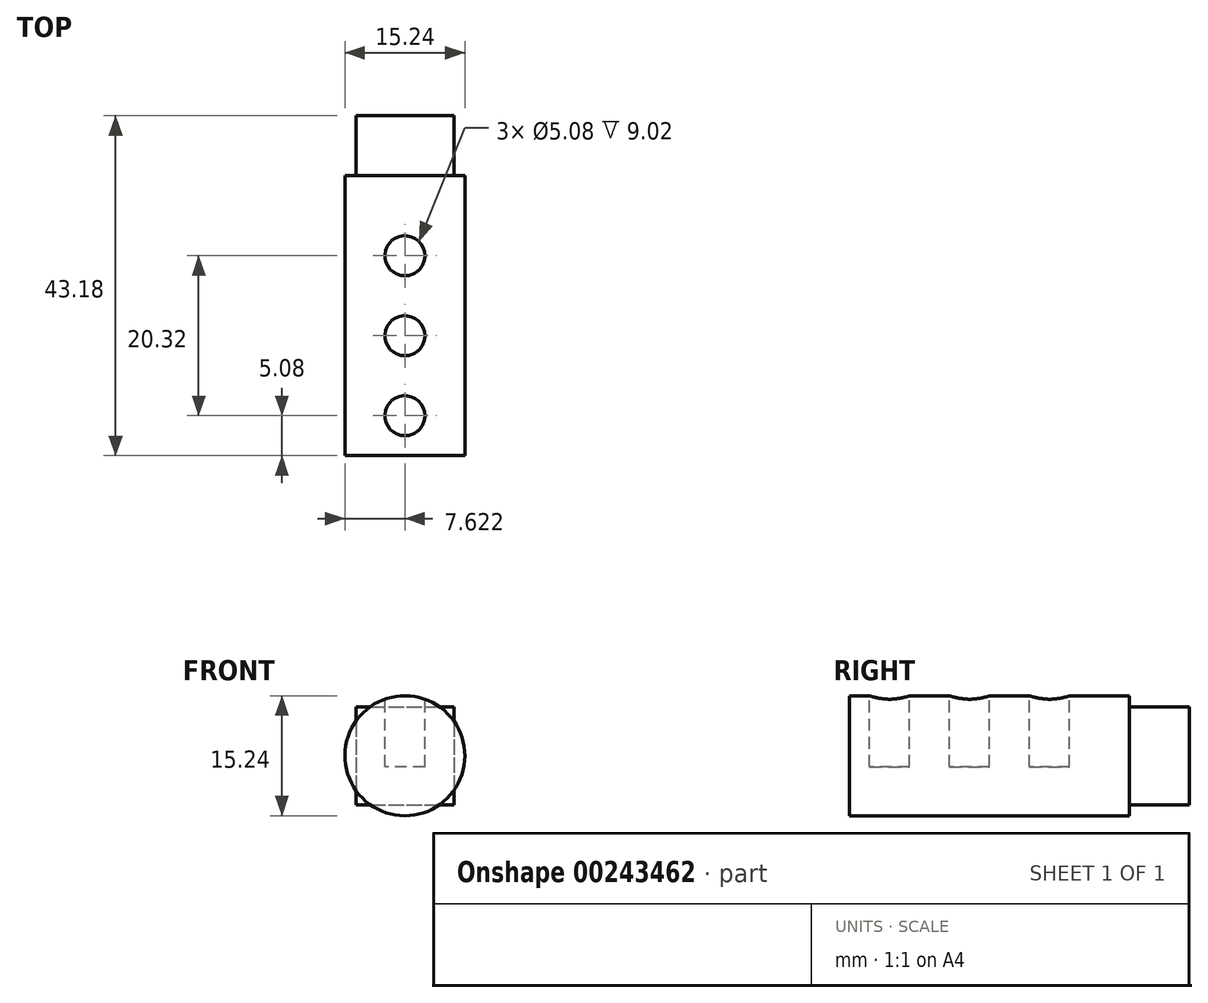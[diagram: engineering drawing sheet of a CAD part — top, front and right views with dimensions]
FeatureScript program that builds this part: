
annotation { "Feature Type Name" : "Feature", "Feature Type Description" : "" }
export const myFeature = defineFeature(function(context is Context, id is Id, definition is map)
    precondition{}
    {
        {
            var Q0;
            Q0=qCreatedBy(makeId("Front.planeOp"),FACE);
            var sketch = newSketch(context, id + "F0", { "sketchPlane" : qUnion([Q0])});
            skLineSegment(sketch, "E0.bottom", {"start": v(-37.58, 42.63) * mm, "end": v(-25.13, 42.63) * mm});
            skLineSegment(sketch, "E0.top", {"start": v(-37.58, 30.18) * mm, "end": v(-25.13, 30.18) * mm});
            skLineSegment(sketch, "E0.left", {"start": v(-37.58, 42.63) * mm, "end": v(-37.58, 30.18) * mm});
            skLineSegment(sketch, "E0.right", {"start": v(-25.13, 42.63) * mm, "end": v(-25.13, 30.18) * mm});
            skSolve(sketch);
        }
        {
            var Q0;
            Q0 = qSketchRegion(id + "F0", true);
            extrude(context, id + "F1", {"entities" : qUnion([Q0]), "depth" : 7.62 * mm});
        }
        {
            var Q0;
            Q0=makeQuery(id+"F1.opExtrude","CAP_FACE",FACE,{"disambiguationData":[OSD([sQuery(id+"F0.wireOp",EDGE,"E0.bottom"),sQuery(id+"F0.wireOp",EDGE,"E0.top"),sQuery(id+"F0.wireOp",EDGE,"E0.left"),sQuery(id+"F0.wireOp",EDGE,"E0.right")])],"isStart":false});
            var sketch = newSketch(context, id + "F2", { "sketchPlane" : qUnion([Q0])});
            skCircle(sketch, "E1", {"center": v(-31.36, 36.4) * mm, "radius": 7.62 * mm});
            skPoint(sketch, "E1.centerSnap0", {"position": v(-31.36, 42.63) * mm});
            skPoint(sketch, "E1.centerSnap1", {"position": v(-25.13, 36.4) * mm});
            skSolve(sketch);
        }
        {
            var Q0;
            Q0 = qSketchRegion(id + "F2", true);
            extrude(context, id + "F3", {"entities" : qUnion([Q0]), "operationType" : NewBodyOperationType.ADD, "depth" : 35.56 * mm});
        }
        {
            var Q0;
            Q0=makeQuery(id+"F1.opExtrude","SWEPT_FACE",FACE,{"disambiguationData":[OSD([sQuery(id+"F0.wireOp",EDGE,"E0.bottom")])]});
            var sketch = newSketch(context, id + "F4", { "sketchPlane" : qUnion([Q0])});
            skCircle(sketch, "E2", {"center": v(-31.36, -17.78) * mm, "radius": 2.54 * mm});
            skCircle(sketch, "E3", {"center": v(-31.36, -27.94) * mm, "radius": 2.54 * mm});
            skCircle(sketch, "E4", {"center": v(-31.36, -38.1) * mm, "radius": 2.54 * mm});
            skSolve(sketch);
        }
        {
            var Q0;
            Q0 = qSketchRegion(id + "F4", true);
            extrude(context, id + "F5", {"entities" : qUnion([Q0]), "operationType" : NewBodyOperationType.REMOVE, "oppositeDirection" : true, "depth" : 7.62 * mm, "hasSecondDirection" : true, "secondDirectionOppositeDirection" : false, "secondDirectionDepth" : 25.4 * mm});
        }
    });
